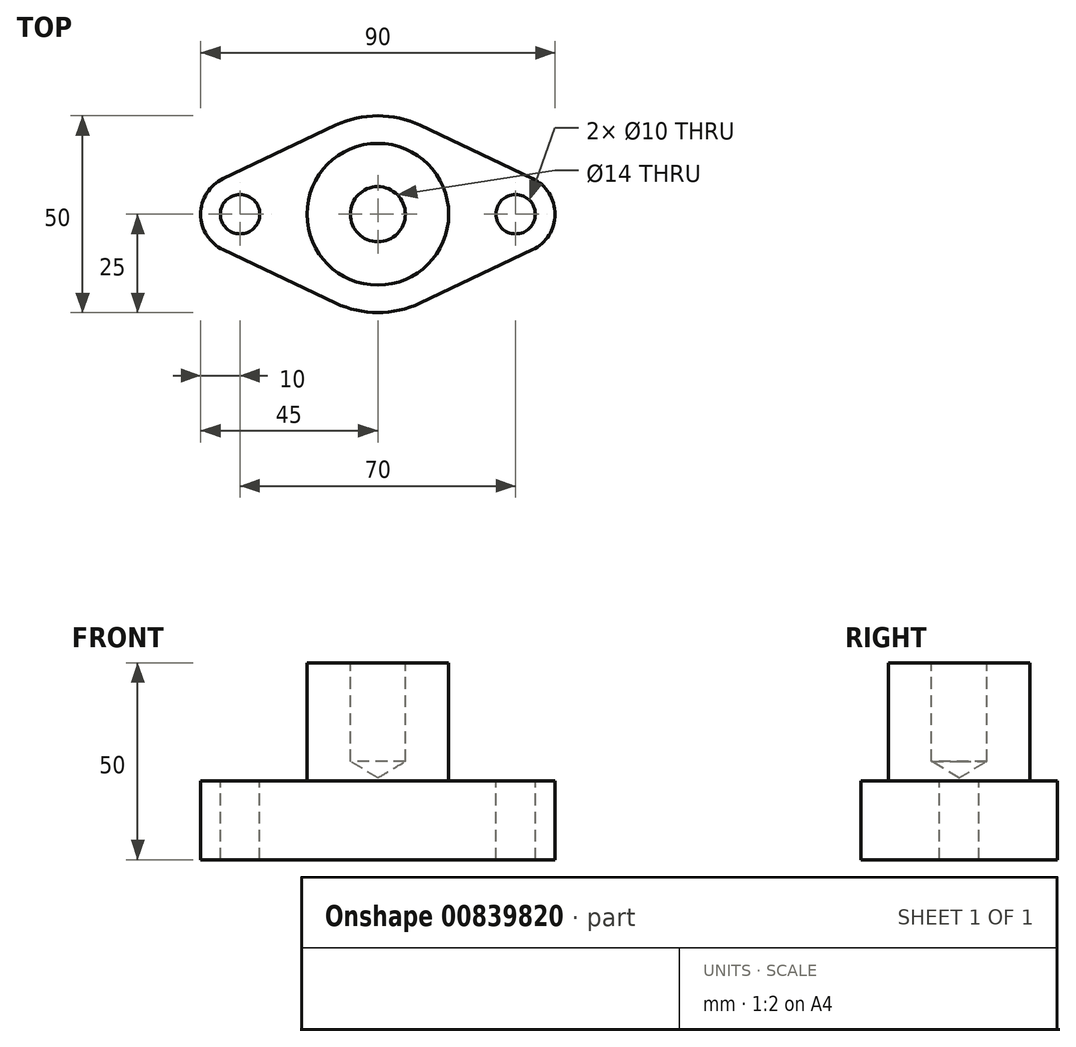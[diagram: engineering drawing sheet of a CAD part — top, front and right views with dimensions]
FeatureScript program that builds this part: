
annotation { "Feature Type Name" : "Feature", "Feature Type Description" : "" }
export const myFeature = defineFeature(function(context is Context, id is Id, definition is map)
    precondition{}
    {
        {
            var Q0;
            Q0=qCreatedBy(makeId("Top.planeOp"),FACE);
            var sketch = newSketch(context, id + "F0", { "sketchPlane" : qUnion([Q0])});
            skArc(sketch, "E0", {"start": v(-10.71, -22.59) * mm, "mid": v(0, -25) * mm, "end": v(10.71, -22.59) * mm});
            skArc(sketch, "E1", {"start": v(-39.29, 9.04) * mm, "mid": v(-45, 0) * mm, "end": v(-39.29, -9.04) * mm});
            skArc(sketch, "E2", {"start": v(39.29, -9.04) * mm, "mid": v(45, 0) * mm, "end": v(39.29, 9.04) * mm});
            skLineSegment(sketch, "E3", {"start": v(10.71, -22.59) * mm, "end": v(39.29, -9.04) * mm});
            skLineSegment(sketch, "E4.trimOffspring", {"start": v(-39.29, 9.04) * mm, "end": v(-10.71, 22.59) * mm});
            skLineSegment(sketch, "E5.trimOffspring", {"start": v(-39.29, -9.04) * mm, "end": v(-10.71, -22.59) * mm});
            skLineSegment(sketch, "E6.trimOffspring", {"start": v(10.71, 22.59) * mm, "end": v(39.29, 9.04) * mm});
            skPoint(sketch, "E7.trimOffspring.start.orphan", {"position": v(58.33, 0) * mm});
            skArc(sketch, "E8.trimOffspring", {"start": v(10.71, 22.59) * mm, "mid": v(0, 25) * mm, "end": v(-10.71, 22.59) * mm});
            skSolve(sketch);
        }
        {
            var Q0;
            Q0=makeQuery(id+"F0.imprint","IMPRINT",FACE,{"disambiguationData":[TD([[makeQuery(id+"F0.imprint","IMPRINT",EDGE,{"derivedFrom":sQuery(id+"F0.wireOp",EDGE,"E0")}),1.0]])]});
            extrude(context, id + "F1", {"entities" : qUnion([Q0]), "endBound" : BoundingType.SYMMETRIC, "depth" : 20 * mm, "offsetDistance" : 25 * mm});
        }
        {
            var Q0;
            Q0=makeQuery(id+"F1.opExtrude","CAP_FACE",FACE,{"disambiguationData":[OSD([sQuery(id+"F0.wireOp",EDGE,"E0"),sQuery(id+"F0.wireOp",EDGE,"E1"),sQuery(id+"F0.wireOp",EDGE,"E2"),sQuery(id+"F0.wireOp",EDGE,"E3"),sQuery(id+"F0.wireOp",EDGE,"E4.trimOffspring"),sQuery(id+"F0.wireOp",EDGE,"E5.trimOffspring"),sQuery(id+"F0.wireOp",EDGE,"E6.trimOffspring"),sQuery(id+"F0.wireOp",EDGE,"E8.trimOffspring")])],"isStart":false});
            var sketch = newSketch(context, id + "F2", { "sketchPlane" : qUnion([Q0])});
            skCircle(sketch, "E9", {"center": v(0, 0) * mm, "radius": 18 * mm});
            skPoint(sketch, "E10", {"position": v(-35, 0) * mm});
            skPoint(sketch, "E11", {"position": v(35, 0) * mm});
            skSolve(sketch);
        }
        {
            var Q0;
            Q0=makeQuery(id+"F2.imprint","IMPRINT",FACE,{"disambiguationData":[TD([[makeQuery(id+"F2.imprint","IMPRINT",EDGE,{"derivedFrom":sQuery(id+"F2.wireOp",EDGE,"E9")}),1.0]])]});
            extrude(context, id + "F3", {"entities" : qUnion([Q0]), "operationType" : NewBodyOperationType.ADD, "depth" : 30 * mm, "offsetDistance" : 25 * mm});
        }
        {
            var Q0;
            Q0=makeQuery(id+"F3.opExtrude","CAP_FACE",FACE,{"disambiguationData":[OSD([sQuery(id+"F2.wireOp",EDGE,"E9")])],"isStart":false});
            var sketch = newSketch(context, id + "F4", { "sketchPlane" : qUnion([Q0])});
            skPoint(sketch, "E12", {"position": v(0, 0) * mm});
            skSolve(sketch);
        }
        {
            var Q0;
            Q0=sQuery(id+"F4.wireOp",VERTEX,"E12");
            var Q1;
            Q1=makeQuery(id+"F1.opExtrude","SWEPT_BODY",BODY,{"disambiguationData":[OSD([sQuery(id+"F0.wireOp",EDGE,"E0"),sQuery(id+"F0.wireOp",EDGE,"E1"),sQuery(id+"F0.wireOp",EDGE,"E2"),sQuery(id+"F0.wireOp",EDGE,"E3"),sQuery(id+"F0.wireOp",EDGE,"E4.trimOffspring"),sQuery(id+"F0.wireOp",EDGE,"E5.trimOffspring"),sQuery(id+"F0.wireOp",EDGE,"E6.trimOffspring"),sQuery(id+"F0.wireOp",EDGE,"E8.trimOffspring")])]});
            hole(context, id + "F5", {"style" : HoleStyle.SIMPLE, "endStyle" : HoleEndStyle.BLIND, "standardTappedOrClearance" : lookupTablePath({ "standard" : "ISO", "engagement" : "75%", "pitch" : "2 mm", "size" : "M16", "type" : "Tapped" }), "standardBlindInLast" : lookupTablePath({ "standard" : "ISO", "engagement" : "75%", "pitch" : "2 mm", "size" : "M16", "type" : "Tapped" }), "holeDiameter" : 14 * mm, "majorDiameter" : 16 * mm, "showTappedDepth" : true, "holeDepth" : 25 * mm, "isTappedThrough" : true, "tappedDepth" : 19 * mm, "tapClearance" : 3, "locations" : qUnion([Q0]), "scope" : qUnion([Q1])});
        }
        {
            var Q0;
            Q0=makeQuery(id+"F1.opExtrude","CAP_FACE",FACE,{"disambiguationData":[OSD([sQuery(id+"F0.wireOp",EDGE,"E0"),sQuery(id+"F0.wireOp",EDGE,"E1"),sQuery(id+"F0.wireOp",EDGE,"E2"),sQuery(id+"F0.wireOp",EDGE,"E3"),sQuery(id+"F0.wireOp",EDGE,"E4.trimOffspring"),sQuery(id+"F0.wireOp",EDGE,"E5.trimOffspring"),sQuery(id+"F0.wireOp",EDGE,"E6.trimOffspring"),sQuery(id+"F0.wireOp",EDGE,"E8.trimOffspring")])],"isStart":false});
            var sketch = newSketch(context, id + "F6", { "sketchPlane" : qUnion([Q0])});
            skPoint(sketch, "E13", {"position": v(-35, 0) * mm});
            skPoint(sketch, "E14", {"position": v(35, 0) * mm});
            skSolve(sketch);
        }
        {
            var Q0;
            Q0=sQuery(id+"F6.wireOp",VERTEX,"E13");
            var Q1;
            Q1=sQuery(id+"F6.wireOp",VERTEX,"E14");
            var Q2;
            Q2=makeQuery(id+"F1.opExtrude","SWEPT_BODY",BODY,{"disambiguationData":[OSD([sQuery(id+"F0.wireOp",EDGE,"E0"),sQuery(id+"F0.wireOp",EDGE,"E1"),sQuery(id+"F0.wireOp",EDGE,"E2"),sQuery(id+"F0.wireOp",EDGE,"E3"),sQuery(id+"F0.wireOp",EDGE,"E4.trimOffspring"),sQuery(id+"F0.wireOp",EDGE,"E5.trimOffspring"),sQuery(id+"F0.wireOp",EDGE,"E6.trimOffspring"),sQuery(id+"F0.wireOp",EDGE,"E8.trimOffspring")])]});
            hole(context, id + "F7", {"style" : HoleStyle.SIMPLE, "endStyle" : HoleEndStyle.BLIND, "holeDiameter" : 10 * mm, "majorDiameter" : 16 * mm, "holeDepth" : 20 * mm, "isTappedThrough" : true, "tappedDepth" : 19 * mm, "tapClearance" : 3, "locations" : qUnion([Q0, Q1]), "scope" : qUnion([Q2])});
        }
    });
